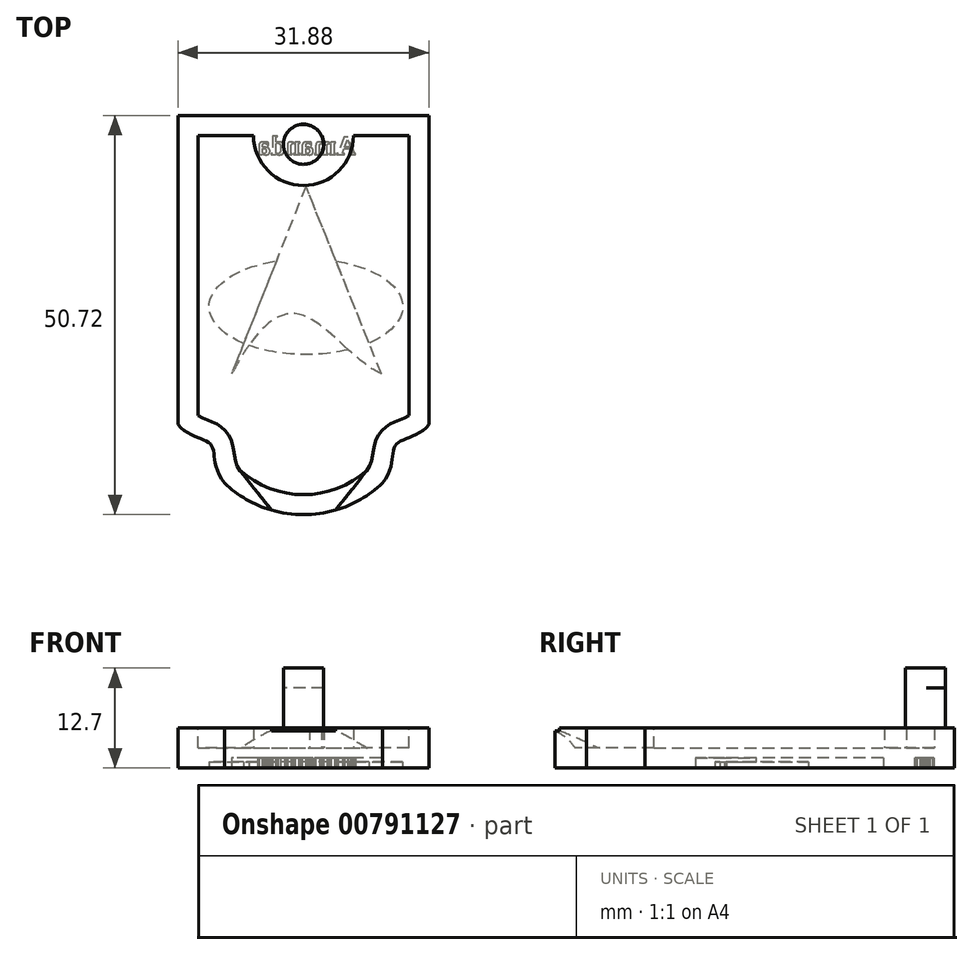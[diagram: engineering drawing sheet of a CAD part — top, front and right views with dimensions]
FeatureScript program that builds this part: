
annotation { "Feature Type Name" : "Feature", "Feature Type Description" : "" }
export const myFeature = defineFeature(function(context is Context, id is Id, definition is map)
    precondition{}
    {
        {
            var Q0;
            Q0=qCreatedBy(makeId("Top.planeOp"),FACE);
            var sketch = newSketch(context, id + "F0", { "sketchPlane" : qUnion([Q0])});
            skLineSegment(sketch, "E0.top", {"start": v(15.94, 23.36) * mm, "end": v(-15.94, 23.36) * mm});
            skLineSegment(sketch, "E0.left", {"start": v(15.94, -15.92) * mm, "end": v(15.94, 23.36) * mm});
            skLineSegment(sketch, "E0.right", {"start": v(-15.94, -15.92) * mm, "end": v(-15.94, 23.36) * mm});
            skPoint(sketch, "E0.middle", {"position": v(0, 0) * mm});
            skFitSpline(sketch, "E1", {"points": [v(-15.94, -15.92) * mm, v(-11.76, -18.47) * mm, v(-10.03, -23.36) * mm], "startDerivative": vector(8.42, -10.11) * mm, "endDerivative": vector(10.16, -12.85) * mm});
            skFitSpline(sketch, "E2.MirrorCS", {"points": [v(15.94, -15.92) * mm, v(11.76, -18.47) * mm, v(10.03, -23.36) * mm], "startDerivative": vector(-8.42, -10.11) * mm, "endDerivative": vector(-10.16, -12.85) * mm});
            skPoint(sketch, "E3.orphan", {"position": v(-15.94, -23.36) * mm});
            skPoint(sketch, "E4.orphan", {"position": v(15.94, -23.36) * mm});
            skArc(sketch, "E5", {"start": v(-10.03, -23.36) * mm, "mid": v(0, -27.36) * mm, "end": v(10.03, -23.36) * mm});
            skSolve(sketch);
        }
        {
            var Q0;
            Q0 = qSketchRegion(id + "F0", true);
            extrude(context, id + "F1", {"entities" : qUnion([Q0]), "oppositeDirection" : true, "depth" : 5.08 * mm, "offsetDistance" : 25.4 * mm});
        }
        {
            var Q0;
            Q0=makeQuery(id+"F1.opExtrude","CAP_FACE",FACE,{"disambiguationData":[OSD([sQuery(id+"F0.wireOp",EDGE,"E0.bottom"),sQuery(id+"F0.wireOp",EDGE,"E0.top"),sQuery(id+"F0.wireOp",EDGE,"E0.left"),sQuery(id+"F0.wireOp",EDGE,"E0.right")])],"isStart":true});
            var sketch = newSketch(context, id + "F2", { "sketchPlane" : qUnion([Q0])});
            skCircle(sketch, "E6", {"center": v(0, 19.68) * mm, "radius": 2.54 * mm});
            skSolve(sketch);
        }
        {
            var Q0;
            Q0 = qSketchRegion(id + "F2", true);
            extrude(context, id + "F3", {"entities" : qUnion([Q0]), "operationType" : NewBodyOperationType.ADD, "depth" : 7.62 * mm, "offsetDistance" : 25.4 * mm});
        }
        {
            var Q0;
            Q0=makeQuery(id+"F1.opExtrude","CAP_FACE",FACE,{"disambiguationData":[OSD([sQuery(id+"F0.wireOp",EDGE,"E0.top"),sQuery(id+"F0.wireOp",EDGE,"E0.left"),sQuery(id+"F0.wireOp",EDGE,"E0.right"),sQuery(id+"F0.wireOp",EDGE,"E1"),sQuery(id+"F0.wireOp",EDGE,"E2.MirrorCS"),sQuery(id+"F0.wireOp",EDGE,"E5")])],"isStart":true});
            shell(context, id + "F4", {"entities" : qUnion([Q0]), "thickness" : 2.54 * mm});
        }
        {
            var Q0;
            {var subQ0=sQuery(id+"F0.wireOp",EDGE,"E5");var subQ1=sQuery(id+"F0.wireOp",EDGE,"E2.MirrorCS");var subQ2=sQuery(id+"F0.wireOp",EDGE,"E1");var subQ3=sQuery(id+"F0.wireOp",EDGE,"E0.right");var subQ4=sQuery(id+"F0.wireOp",EDGE,"E0.left");var subQ5=sQuery(id+"F0.wireOp",EDGE,"E0.top");Q0=makeQuery(id+"F4.opShell","OFFSET_FACE",FACE,{"disambiguationData":[OSD([subQ5,subQ4,subQ3,subQ2,subQ1,subQ0]),TDD([makeQuery(id+"F1.opExtrude","CAP_FACE",FACE,{"disambiguationData":[OSD([subQ5,subQ4,subQ3,subQ2,subQ1,subQ0])],"isStart":false})])]});}
            var sketch = newSketch(context, id + "F5", { "sketchPlane" : qUnion([Q0])});
            skArc(sketch, "E7", {"start": v(-6.35, 20.82) * mm, "mid": v(0, 14.47) * mm, "end": v(6.35, 20.82) * mm});
            skArc(sketch, "E8", {"start": v(-2.2, 20.82) * mm, "mid": v(0.07, 17.18) * mm, "end": v(2.34, 20.82) * mm});
            skLineSegment(sketch, "E9", {"start": v(-2.2, 20.82) * mm, "end": v(-6.35, 20.82) * mm});
            skLineSegment(sketch, "E10", {"start": v(6.35, 20.82) * mm, "end": v(2.34, 20.82) * mm});
            skSolve(sketch);
        }
        {
            var Q0;
            Q0 = qSketchRegion(id + "F5", true);
            extrude(context, id + "F6", {"entities" : qUnion([Q0]), "operationType" : NewBodyOperationType.ADD, "depth" : 2.54 * mm, "offsetDistance" : 25.4 * mm});
        }
        {
            var Q0;
            {var subQ0=sQuery(id+"F0.wireOp",EDGE,"E5");var subQ1=sQuery(id+"F0.wireOp",EDGE,"E2.MirrorCS");var subQ2=sQuery(id+"F0.wireOp",EDGE,"E1");var subQ3=sQuery(id+"F0.wireOp",EDGE,"E0.right");var subQ4=sQuery(id+"F0.wireOp",EDGE,"E0.left");var subQ5=sQuery(id+"F0.wireOp",EDGE,"E0.top");Q0=makeQuery(id+"F4.opShell","OFFSET_FACE",FACE,{"disambiguationData":[OSD([subQ5,subQ4,subQ3,subQ2,subQ1,subQ0]),TDD([makeQuery(id+"F1.opExtrude","CAP_FACE",FACE,{"disambiguationData":[OSD([subQ5,subQ4,subQ3,subQ2,subQ1,subQ0])],"isStart":false})])]});}
            var sketch = newSketch(context, id + "F7", { "sketchPlane" : qUnion([Q0])});
            skCircle(sketch, "E11", {"center": v(0, 19.7) * mm, "radius": 2.54 * mm});
            skSolve(sketch);
        }
        {
            var Q0;
            Q0 = qSketchRegion(id + "F7", true);
            extrude(context, id + "F8", {"entities" : qUnion([Q0]), "operationType" : NewBodyOperationType.ADD, "depth" : 7.62 * mm, "offsetDistance" : 25.4 * mm});
        }
        {
            var Q0;
            {var subQ0=sQuery(id+"F0.wireOp",EDGE,"E5");Q0=makeQuery(id+"F4.opShell","OFFSET_EDGE",EDGE,{"disambiguationData":[OSD([subQ0]),TDD([makeQuery(id+"F1.opExtrude","CAP_EDGE",EDGE,{"disambiguationData":[OSD([subQ0])],"isStart":true})])]});}
            fillet(context, id + "F9", {"entities" : qUnion([Q0]), "radius" : 5.08 * mm, "tangentPropagation" : true, "allowEdgeOverflow" : false});
        }
        {
            var Q0;
            Q0=makeQuery(id+"F1.opExtrude","CAP_FACE",FACE,{"disambiguationData":[OSD([sQuery(id+"F0.wireOp",EDGE,"E0.top"),sQuery(id+"F0.wireOp",EDGE,"E0.left"),sQuery(id+"F0.wireOp",EDGE,"E0.right"),sQuery(id+"F0.wireOp",EDGE,"E1"),sQuery(id+"F0.wireOp",EDGE,"E2.MirrorCS"),sQuery(id+"F0.wireOp",EDGE,"E5")])],"isStart":false});
            var sketch = newSketch(context, id + "F10", { "sketchPlane" : qUnion([Q0])});
            skText(sketch, "E12", { "text": "Amanda", "fontName": "Tinos-Bold.ttf"});
            skLineSegment(sketch, "E13", {"start": v(9.9, 9.5) * mm, "end": v(0.31, -14.36) * mm});
            skLineSegment(sketch, "E14", {"start": v(0.31, -14.36) * mm, "end": v(-9.14, 9.5) * mm});
            skFitSpline(sketch, "E15", {"points": [v(9.9, 9.5) * mm, v(-9.14, 9.5) * mm], "startDerivative": vector(-21.36, -10.56) * mm, "endDerivative": vector(-24.64, 46.06) * mm});
            skEllipticalArc(sketch, "E16", {});
            skEllipticalArc(sketch, "E17.trimOffspring", {});
            skEllipticalArc(sketch, "E18.trimOffspring", {});
            const initialGuessF10  = {"E12": [0.00666, -0.01838, -1, 0, 0.00246], "E16": [0.00031470241252041066, 0.0009341798722743953, -1, 0, 0.012294684536755085, 0.006094106571312917, 5.411569815407148, 1.2596500863328615], "E17.trimOffspring": [0.00031470241252041066, 0.0009341798722743953, -1, 0, 0.012294684536755085, 0.006094106571312917, 4.2596733084288925, 5.34322991153381], "E18.trimOffspring": [0.00031470241252041066, 0.0009341798722743953, -1, 0, 0.012294684536755085, 0.006094106571312917, 1.8867642181982713, 4.0030869742612545]};
            skSetInitialGuess(sketch, initialGuessF10);
            skSolve(sketch);
        }
        {
            var Q0;
            {var subQ1=sQuery(id+"F10.wireOp",EDGE,"E13");var subQ8=sQuery(id+"F10.wireOp",EDGE,"E15");var subQ9=makeQuery(id+"F10.imprint","INTERSECT",VERTEX,{"derivedFrom":[subQ1,subQ8]});Q0=makeQuery(id+"F10.imprint","IMPRINT",FACE,{"disambiguationData":[TD([[makeQuery(id+"F10.imprint","IMPRINT",EDGE,{"disambiguationData":[TD([[subQ9,-1.0]])],"derivedFrom":subQ1}),-1.0]])]});}
            var Q1;
            Q1=makeQuery(id+"F10.imprint","IMPRINT",FACE,{"disambiguationData":[TD([[makeQuery(id+"F10.imprint","IMPRINT",EDGE,{"derivedFrom":sQuery(id+"F10.wireOp",EDGE,"E12.sketch_text.stroke-56")}),-1.0]])]});
            var Q2;
            Q2=makeQuery(id+"F10.imprint","IMPRINT",FACE,{"disambiguationData":[TD([[makeQuery(id+"F10.imprint","IMPRINT",EDGE,{"derivedFrom":sQuery(id+"F10.wireOp",EDGE,"E12.sketch_text.stroke-19")}),-1.0]])]});
            var Q3;
            Q3=makeQuery(id+"F10.imprint","IMPRINT",FACE,{"disambiguationData":[TD([[makeQuery(id+"F10.imprint","IMPRINT",EDGE,{"derivedFrom":sQuery(id+"F10.wireOp",EDGE,"E12.sketch_text.stroke-0")}),-1.0]])]});
            var Q4;
            Q4=makeQuery(id+"F10.imprint","IMPRINT",FACE,{"disambiguationData":[TD([[makeQuery(id+"F10.imprint","IMPRINT",EDGE,{"derivedFrom":sQuery(id+"F10.wireOp",EDGE,"E12.sketch_text.stroke-84")}),-1.0]])]});
            var Q5;
            Q5=makeQuery(id+"F10.imprint","IMPRINT",FACE,{"disambiguationData":[TD([[makeQuery(id+"F10.imprint","IMPRINT",EDGE,{"derivedFrom":sQuery(id+"F10.wireOp",EDGE,"E12.sketch_text.stroke-108")}),-1.0]])]});
            var Q6;
            Q6=makeQuery(id+"F10.imprint","IMPRINT",FACE,{"disambiguationData":[TD([[makeQuery(id+"F10.imprint","IMPRINT",EDGE,{"derivedFrom":sQuery(id+"F10.wireOp",EDGE,"E12.sketch_text.stroke-133")}),-1.0]])]});
            extrude(context, id + "F11", {"entities" : qUnion([Q0, Q1, Q2, Q3, Q4, Q5, Q6]), "operationType" : NewBodyOperationType.REMOVE, "oppositeDirection" : true, "depth" : 1.27 * mm, "offsetDistance" : 25.4 * mm});
        }
        {
            var Q0;
            {var subQ0=sQuery(id+"F10.wireOp",EDGE,"E17.trimOffspring");Q0=makeQuery(id+"F10.imprint","IMPRINT",FACE,{"disambiguationData":[TD([[makeQuery(id+"F10.imprint","IMPRINT",EDGE,{"derivedFrom":subQ0}),1.0]])]});}
            var Q1;
            {var subQ0=sQuery(id+"F10.wireOp",EDGE,"E18.trimOffspring");Q1=makeQuery(id+"F10.imprint","IMPRINT",FACE,{"disambiguationData":[TD([[makeQuery(id+"F10.imprint","IMPRINT",EDGE,{"derivedFrom":subQ0}),1.0]])]});}
            var Q2;
            {var subQ0=sQuery(id+"F10.wireOp",EDGE,"E16");Q2=makeQuery(id+"F10.imprint","IMPRINT",FACE,{"disambiguationData":[TD([[makeQuery(id+"F10.imprint","IMPRINT",EDGE,{"derivedFrom":subQ0}),1.0]])]});}
            extrude(context, id + "F12", {"entities" : qUnion([Q0, Q1, Q2]), "operationType" : NewBodyOperationType.REMOVE, "oppositeDirection" : true, "depth" : 0.76 * mm, "offsetDistance" : 25.4 * mm});
        }
    });
